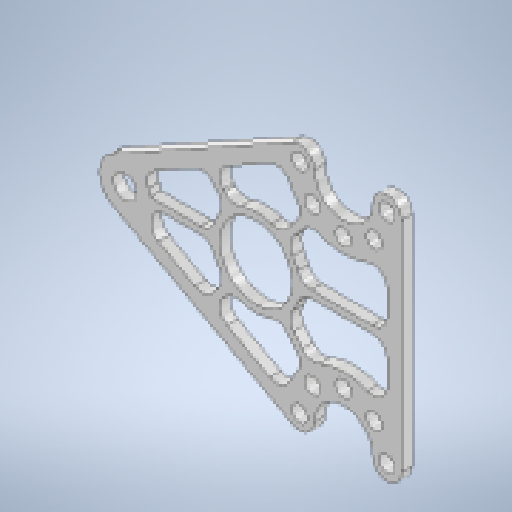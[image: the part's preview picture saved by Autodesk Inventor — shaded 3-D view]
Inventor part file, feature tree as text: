
AUTODESK INVENTOR PART (.ipt)
format: ipt  version: 2025.1 (Build 291241000, 241)  size: 323,072 bytes
history: native  units: mm
features: other x2, extrude x2, sketch x2, fillet x1, projected_geometry x1
ambient origin geometry x8: Origin, YZ Plane, XZ Plane, XY Plane, X Axis, Y Axis, Z Axis, Center Point
bodies: Body1 (feature_tree)
feature tree (8):
  other  "ソリッド1"
  extrude  "押し出し1"  Depth=8.0mm
  extrude  "押し出し3"  Depth=16.0mm
  fillet  "フィレット2"  Radius=12.0mm
  sketch  "スケッチ1"
  other  "スケッチ円形状パターン1"
  sketch  "スケッチ3"
  projected_geometry  "投影ループ2"
